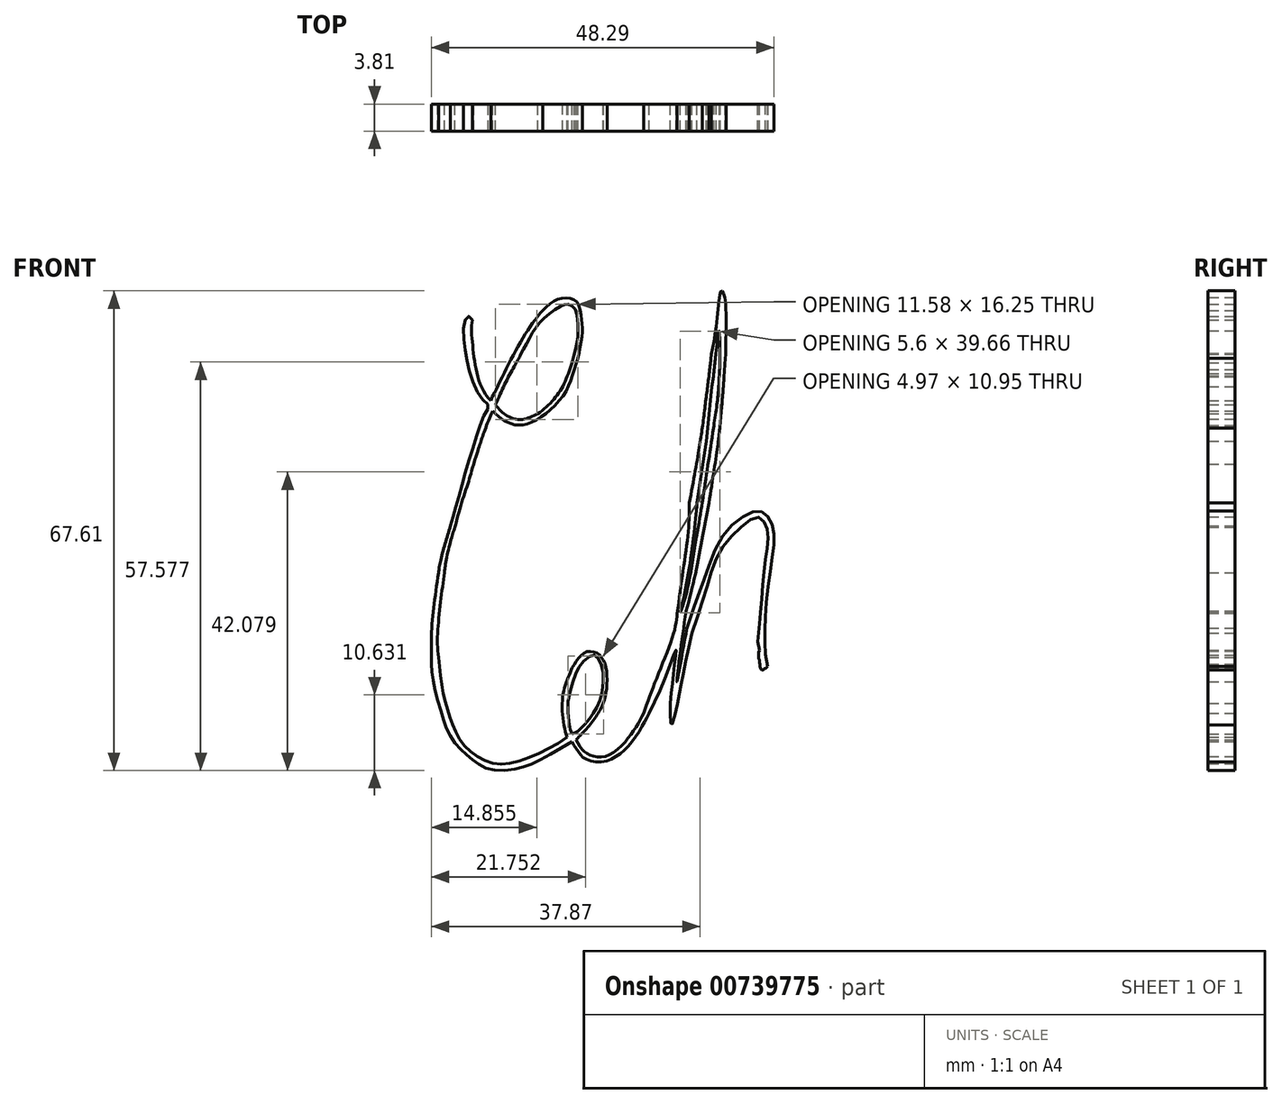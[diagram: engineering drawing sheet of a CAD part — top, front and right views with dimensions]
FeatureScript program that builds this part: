
annotation { "Feature Type Name" : "Feature", "Feature Type Description" : "" }
export const myFeature = defineFeature(function(context is Context, id is Id, definition is map)
    precondition{}
    {
        {
            var Q0;
            Q0=qCreatedBy(makeId("Front.planeOp"),FACE);
            var sketch = newSketch(context, id + "F0", { "sketchPlane" : qUnion([Q0])});
            skFitSpline(sketch, "E0", {"points": [v(-64.35, 36.4) * mm, v(-64.4, 33.61) * mm, v(-63.78, 29.13) * mm, v(-61.8, 25.09) * mm], "startDerivative": vector(-2.62, -8.07) * mm, "endDerivative": vector(9.26, -9.07) * mm});
            skFitSpline(sketch, "E1", {"points": [v(-64.35, 36.4) * mm, v(-64.98, 36.94) * mm, v(-65.59, 35.64) * mm, v(-65.34, 32.1) * mm, v(-64.6, 28.52) * mm, v(-62.99, 25.26) * mm, v(-62.14, 24.35) * mm, v(-62.62, 23.14) * mm, v(-63.9, 19.7) * mm, v(-65.4, 14.73) * mm, v(-66.62, 10.38) * mm, v(-67.46, 7.41) * mm], "startDerivative": vector(-16.96, 17.03) * mm, "endDerivative": vector(-8.5, -29.3) * mm});
            skFitSpline(sketch, "E2", {"points": [v(-61.8, 25.09) * mm, v(-59.74, 29.26) * mm, v(-56.96, 34.37) * mm, v(-54.45, 37.79) * mm], "startDerivative": vector(5.82, 11.78) * mm, "endDerivative": vector(8.75, 9.95) * mm});
            skFitSpline(sketch, "E3", {"points": [v(-61.53, 23.57) * mm, v(-62.96, 19.97) * mm, v(-64.2, 16.13) * mm], "startDerivative": vector(-3.47, -7.39) * mm, "endDerivative": vector(-4.23, -13.44) * mm});
            skFitSpline(sketch, "E4", {"points": [v(-64.2, 16.13) * mm, v(-64.92, 13.64) * mm, v(-65.9, 10.66) * mm, v(-66.63, 8.04) * mm, v(-66.83, 7.2) * mm], "startDerivative": vector(-3.72, -12.5) * mm, "endDerivative": vector(-1.05, -4.59) * mm});
            skFitSpline(sketch, "E5", {"points": [v(-61.1, 24.48) * mm, v(-59.66, 27.69) * mm, v(-58.31, 30.15) * mm, v(-57.6, 31.45) * mm], "startDerivative": vector(3.5, 8.33) * mm, "endDerivative": vector(2.51, 4.74) * mm});
            skFitSpline(sketch, "E6", {"points": [v(-61.1, 24.48) * mm, v(-59.62, 23) * mm, v(-57.22, 22.4) * mm, v(-55.13, 23.2) * mm], "startDerivative": vector(4.05, -5.34) * mm, "endDerivative": vector(6.73, 2.03) * mm});
            skFitSpline(sketch, "E7", {"points": [v(-61.53, 23.57) * mm, v(-60.22, 22.47) * mm, v(-58.91, 21.78) * mm, v(-57.12, 21.66) * mm, v(-54.44, 22.94) * mm, v(-51.5, 25.91) * mm, v(-50.02, 29.46) * mm], "startDerivative": vector(9.66, -8.64) * mm, "endDerivative": vector(5.16, 19.12) * mm});
            skFitSpline(sketch, "E8", {"points": [v(-55.13, 23.2) * mm, v(-52.99, 25.14) * mm, v(-51.45, 27.47) * mm, v(-50.36, 30.38) * mm], "startDerivative": vector(6.93, 4.81) * mm, "endDerivative": vector(2.85, 8.56) * mm});
            skFitSpline(sketch, "E9", {"points": [v(-57.6, 31.45) * mm, v(-56.5, 33.56) * mm, v(-55.39, 35.43) * mm, v(-53.75, 37.14) * mm, v(-51.86, 38.42) * mm, v(-50.98, 38.63) * mm, v(-50.06, 38.2) * mm, v(-49.63, 36.89) * mm, v(-49.5, 35.16) * mm, v(-49.65, 33.16) * mm, v(-50.36, 30.38) * mm], "startDerivative": vector(9.87, 18.84) * mm, "endDerivative": vector(-6.78, -23.18) * mm});
            skFitSpline(sketch, "E10", {"points": [v(-54.45, 37.79) * mm, v(-52.67, 39.23) * mm, v(-50.98, 39.51) * mm, v(-49.63, 38.95) * mm, v(-49.03, 36.89) * mm, v(-48.88, 35.06) * mm, v(-49.18, 32.77) * mm, v(-50.02, 29.46) * mm], "startDerivative": vector(11.6, 11.5) * mm, "endDerivative": vector(-7.3, -17.15) * mm});
            skFitSpline(sketch, "E11", {"points": [v(-67.46, 7.41) * mm, v(-66.83, 7.2) * mm], "startDerivative": vector(0.63, -0.2) * mm, "endDerivative": vector(0.63, -0.2) * mm});
            skFitSpline(sketch, "E12", {"points": [v(-67.46, 7.41) * mm, v(-68.32, 4.56) * mm, v(-68.98, 1.92) * mm, v(-69.14, 0.83) * mm], "startDerivative": vector(-2.23, -7.16) * mm, "endDerivative": vector(-0.43, -4.1) * mm});
            skFitSpline(sketch, "E13", {"points": [v(-66.83, 7.2) * mm, v(-67.46, 5.2) * mm, v(-68.2, 1.84) * mm, v(-68.3, 0.83) * mm], "startDerivative": vector(-1.82, -5.25) * mm, "endDerivative": vector(-0.2, -3.57) * mm});
            skFitSpline(sketch, "E14", {"points": [v(-69.14, 0.83) * mm, v(-69.73, -3.34) * mm, v(-70.1, -6.73) * mm, v(-70.16, -10.09) * mm, v(-70.13, -12.11) * mm], "startDerivative": vector(-2.2, -14.98) * mm, "endDerivative": vector(0.18, -9.47) * mm});
            skFitSpline(sketch, "E15", {"points": [v(-68.3, 0.83) * mm, v(-68.7, -2.07) * mm, v(-69.1, -5.55) * mm, v(-69.3, -8.6) * mm, v(-69.14, -11.16) * mm], "startDerivative": vector(-1.7, -11.4) * mm, "endDerivative": vector(1.4, -10.98) * mm});
            skFitSpline(sketch, "E16", {"points": [v(-70.13, -12.11) * mm, v(-69.84, -14.78) * mm, v(-68.75, -18.95) * mm, v(-67.7, -21.88) * mm, v(-65.97, -24.15) * mm, v(-64.15, -25.73) * mm, v(-61.95, -26.9) * mm, v(-58.2, -26.85) * mm, v(-55.23, -25.79) * mm, v(-50.33, -23) * mm], "startDerivative": vector(1.26, -23.58) * mm, "endDerivative": vector(35.66, 20.71) * mm});
            skFitSpline(sketch, "E17", {"points": [v(-69.14, -11.16) * mm, v(-68.72, -14.84) * mm, v(-67.97, -18.25) * mm, v(-67.06, -20.89) * mm, v(-65.58, -23.49) * mm, v(-62.94, -25.51) * mm, v(-59.95, -26.18) * mm, v(-55.65, -24.94) * mm, v(-51.03, -22.4) * mm], "startDerivative": vector(2.52, -29.28) * mm, "endDerivative": vector(28.6, 20.85) * mm});
            skFitSpline(sketch, "E18", {"points": [v(-51.03, -22.4) * mm, v(-50.33, -23) * mm], "startDerivative": vector(0.6, -0.6) * mm, "endDerivative": vector(0.6, -0.6) * mm});
            skFitSpline(sketch, "E19", {"points": [v(-51.03, -22.4) * mm, v(-51.62, -19.7) * mm, v(-51.6, -16.4) * mm, v(-51.03, -14.36) * mm, v(-50.34, -12.6) * mm], "startDerivative": vector(-2.82, 8.16) * mm, "endDerivative": vector(2.45, 7.62) * mm});
            skFitSpline(sketch, "E20", {"points": [v(-50.33, -21.92) * mm, v(-50.66, -20.9) * mm, v(-50.91, -17.6) * mm, v(-50.05, -14.13) * mm, v(-49.2, -12.27) * mm, v(-47.68, -10.9) * mm, v(-47.04, -10.88) * mm, v(-46.2, -12.12) * mm, v(-45.95, -14.65) * mm, v(-46.59, -17.62) * mm, v(-47.44, -19.13) * mm, v(-48.62, -20.67) * mm, v(-50.33, -21.92) * mm]});
            skFitSpline(sketch, "E21", {"points": [v(-50.34, -12.6) * mm, v(-49.45, -11.32) * mm, v(-48.35, -10.38) * mm, v(-47.11, -10.4) * mm, v(-46.24, -11.04) * mm, v(-45.64, -12.27) * mm, v(-45.4, -14.17) * mm, v(-45.55, -16.11) * mm, v(-45.95, -17.62) * mm], "startDerivative": vector(6.67, 10.14) * mm, "endDerivative": vector(-4.17, -10.58) * mm});
            skFitSpline(sketch, "E22", {"points": [v(-45.95, -17.62) * mm, v(-46.92, -19.43) * mm, v(-48.07, -20.98) * mm, v(-49.17, -22.13) * mm, v(-49.79, -22.74) * mm, v(-50.33, -23) * mm], "startDerivative": vector(-3.31, -8.04) * mm, "endDerivative": vector(-3.52, -1.93) * mm});
            skFitSpline(sketch, "E23", {"points": [v(-49.79, -22.74) * mm, v(-48.83, -24.24) * mm, v(-47.54, -25) * mm, v(-45.45, -25.05) * mm, v(-42.88, -23.06) * mm, v(-41.26, -20.86) * mm, v(-40.25, -19) * mm], "startDerivative": vector(5.87, -10.96) * mm, "endDerivative": vector(4.64, 10.81) * mm});
            skFitSpline(sketch, "E24", {"points": [v(-50.33, -23) * mm, v(-49.5, -24.38) * mm, v(-48.49, -25.41) * mm, v(-46.03, -25.84) * mm, v(-43.55, -24.7) * mm, v(-41.3, -22.2) * mm, v(-39.76, -19.6) * mm, v(-39.46, -19) * mm], "startDerivative": vector(5.98, -12.09) * mm, "endDerivative": vector(3.02, 5.95) * mm});
            skFitSpline(sketch, "E25", {"points": [v(-40.25, -19) * mm, v(-39.46, -19) * mm], "startDerivative": vector(0.86, 0) * mm, "endDerivative": vector(0.86, 0) * mm});
            skFitSpline(sketch, "E26", {"points": [v(-39.46, -19) * mm, v(-37.02, -13.56) * mm, v(-35.69, -10.1) * mm, v(-35.83, -11.76) * mm, v(-36.2, -14.82) * mm, v(-36.52, -18.64) * mm, v(-36.34, -20.65) * mm, v(-35.5, -17.8) * mm, v(-34.83, -14.21) * mm, v(-33.42, -7.73) * mm], "startDerivative": vector(17.31, 35.25) * mm, "endDerivative": vector(10.54, 46.96) * mm});
            skFitSpline(sketch, "E27", {"points": [v(-40.25, -19) * mm, v(-38.42, -14.1) * mm, v(-36.01, -7.73) * mm, v(-35.5, -4.93) * mm], "startDerivative": vector(4.73, 13.2) * mm, "endDerivative": vector(1.04, 9.73) * mm});
            skFitSpline(sketch, "E28", {"points": [v(-34.25, -4.6) * mm, v(-34.83, -8.45) * mm, v(-35.33, -12.3) * mm, v(-35.55, -14.6) * mm, v(-34.97, -11.44) * mm, v(-34.14, -7.02) * mm], "startDerivative": vector(-2.82, -18.55) * mm, "endDerivative": vector(3.5, 17.96) * mm});
            skFitSpline(sketch, "E29", {"points": [v(-33.42, -7.73) * mm, v(-34.14, -7.02) * mm], "startDerivative": vector(-0.72, 0.72) * mm, "endDerivative": vector(-0.72, 0.72) * mm});
            skFitSpline(sketch, "E30", {"points": [v(-35.5, -4.93) * mm, v(-34.25, -4.6) * mm], "startDerivative": vector(1.26, 0.32) * mm, "endDerivative": vector(1.26, 0.32) * mm});
            skFitSpline(sketch, "E31", {"points": [v(-35.5, -4.93) * mm, v(-34.63, 1.5) * mm, v(-33.93, 6.86) * mm, v(-33.81, 10.61) * mm], "startDerivative": vector(2.32, 17.43) * mm, "endDerivative": vector(0.05, 12.66) * mm});
            skFitSpline(sketch, "E32", {"points": [v(-35.1, -4.82) * mm, v(-34.17, -0.64) * mm, v(-33.5, 3.54) * mm, v(-33, 7.86) * mm, v(-32.72, 10.67) * mm], "startDerivative": vector(3.72, 16.02) * mm, "endDerivative": vector(1.14, 12.43) * mm});
            skFitSpline(sketch, "E33", {"points": [v(-35.1, -4.82) * mm, v(-34.26, -2.21) * mm, v(-33.2, 3.23) * mm, v(-32.45, 7.92) * mm, v(-31.97, 10.74) * mm], "startDerivative": vector(3.98, 11.11) * mm, "endDerivative": vector(2.19, 12.4) * mm});
            skFitSpline(sketch, "E34", {"points": [v(-34.25, -4.6) * mm, v(-33.02, 0.36) * mm, v(-31.97, 5.65) * mm, v(-31.06, 10.64) * mm], "startDerivative": vector(3.84, 14.83) * mm, "endDerivative": vector(2.7, 15) * mm});
            skFitSpline(sketch, "E35", {"points": [v(-31.97, 10.74) * mm, v(-30.85, 18.28) * mm, v(-30.42, 21.15) * mm], "startDerivative": vector(2.03, 13.64) * mm, "endDerivative": vector(0.98, 6.64) * mm});
            skFitSpline(sketch, "E36", {"points": [v(-31.06, 10.64) * mm, v(-29.88, 18.28) * mm, v(-29.52, 21.15) * mm], "startDerivative": vector(2.2, 13.78) * mm, "endDerivative": vector(0.78, 6.67) * mm});
            skFitSpline(sketch, "E37", {"points": [v(-32.72, 10.67) * mm, v(-31.42, 19.34) * mm], "startDerivative": vector(1.3, 8.66) * mm, "endDerivative": vector(1.3, 8.66) * mm});
            skFitSpline(sketch, "E38", {"points": [v(-33.81, 10.61) * mm, v(-32.48, 17.98) * mm, v(-31.97, 21.24) * mm], "startDerivative": vector(2.5, 13.48) * mm, "endDerivative": vector(1.1, 7.37) * mm});
            skFitSpline(sketch, "E39", {"points": [v(-31.42, 19.34) * mm, v(-31.2, 21.15) * mm], "startDerivative": vector(0.21, 1.82) * mm, "endDerivative": vector(0.21, 1.82) * mm});
            skFitSpline(sketch, "E40", {"points": [v(-30.42, 21.15) * mm, v(-29.52, 21.15) * mm], "startDerivative": vector(0.9, 0) * mm, "endDerivative": vector(0.9, 0) * mm});
            skFitSpline(sketch, "E41", {"points": [v(-31.97, 21.24) * mm, v(-31.2, 21.15) * mm], "startDerivative": vector(0.76, -0.1) * mm, "endDerivative": vector(0.76, -0.1) * mm});
            skFitSpline(sketch, "E42", {"points": [v(-31.2, 21.15) * mm, v(-30.64, 27.04) * mm], "startDerivative": vector(0.57, 5.88) * mm, "endDerivative": vector(0.57, 5.88) * mm});
            skFitSpline(sketch, "E43", {"points": [v(-31.97, 21.24) * mm, v(-31.46, 25.35) * mm, v(-31.05, 28.44) * mm], "startDerivative": vector(0.96, 7.94) * mm, "endDerivative": vector(0.86, 6.42) * mm});
            skFitSpline(sketch, "E44", {"points": [v(-30.42, 21.15) * mm, v(-29.8, 25.65) * mm, v(-29.58, 28.84) * mm], "startDerivative": vector(1.34, 8.62) * mm, "endDerivative": vector(0.32, 6.69) * mm});
            skFitSpline(sketch, "E45", {"points": [v(-29.52, 21.15) * mm, v(-29.15, 25.44) * mm, v(-28.93, 28.39) * mm], "startDerivative": vector(0.73, 8.2) * mm, "endDerivative": vector(0.43, 6.2) * mm});
            skFitSpline(sketch, "E46", {"points": [v(-30.64, 27.04) * mm, v(-30.42, 28.48) * mm], "startDerivative": vector(0.22, 1.44) * mm, "endDerivative": vector(0.22, 1.44) * mm});
            skFitSpline(sketch, "E47", {"points": [v(-30.42, 28.48) * mm, v(-31.05, 28.44) * mm], "startDerivative": vector(-0.63, -0.04) * mm, "endDerivative": vector(-0.63, -0.04) * mm});
            skFitSpline(sketch, "E48", {"points": [v(-29.58, 28.84) * mm, v(-28.93, 28.39) * mm], "startDerivative": vector(0.65, -0.45) * mm, "endDerivative": vector(0.65, -0.45) * mm});
            skFitSpline(sketch, "E49", {"points": [v(-30.42, 28.48) * mm, v(-30.16, 30.82) * mm, v(-30.06, 31.64) * mm], "startDerivative": vector(0.47, 4.2) * mm, "endDerivative": vector(0.23, 1.93) * mm});
            skFitSpline(sketch, "E50", {"points": [v(-29.58, 28.84) * mm, v(-29.5, 30.49) * mm, v(-29.5, 31.64) * mm], "startDerivative": vector(0.2, 3.16) * mm, "endDerivative": vector(-0.03, 2.42) * mm});
            skFitSpline(sketch, "E51", {"points": [v(-31.05, 28.44) * mm, v(-30.76, 31.1) * mm, v(-30.71, 31.62) * mm], "startDerivative": vector(0.52, 4.58) * mm, "endDerivative": vector(0.1, 1.36) * mm});
            skFitSpline(sketch, "E52", {"points": [v(-28.93, 28.39) * mm, v(-28.73, 31.04) * mm], "startDerivative": vector(0.2, 2.66) * mm, "endDerivative": vector(0.2, 2.66) * mm});
            skFitSpline(sketch, "E53", {"points": [v(-30.06, 31.64) * mm, v(-29.64, 34.9) * mm, v(-29.53, 33.9) * mm, v(-29.5, 31.64) * mm], "startDerivative": vector(1.17, 11.6) * mm, "endDerivative": vector(0.02, -6.52) * mm});
            skFitSpline(sketch, "E54", {"points": [v(-30.71, 31.62) * mm, v(-30.06, 35.34) * mm, v(-29.5, 40.13) * mm, v(-29.28, 40.54) * mm, v(-28.95, 40.13) * mm, v(-28.65, 38.1) * mm, v(-28.64, 35.11) * mm, v(-28.67, 32.38) * mm, v(-28.73, 31.04) * mm], "startDerivative": vector(4.1, 19.52) * mm, "endDerivative": vector(-2.58, -8.46) * mm});
            skFitSpline(sketch, "E55", {"points": [v(-34.14, -7.02) * mm, v(-31.67, 0) * mm, v(-29.2, 5.9) * mm, v(-25.64, 9.03) * mm, v(-23.62, 9.4) * mm, v(-22.35, 8.07) * mm, v(-21.87, 5.7) * mm, v(-22.3, 1.78) * mm, v(-23.01, -4.28) * mm, v(-23.14, -8.73) * mm, v(-22.77, -12.38) * mm], "startDerivative": vector(28.4, 88.34) * mm, "endDerivative": vector(11.15, -39.79) * mm});
            skFitSpline(sketch, "E56", {"points": [v(-33.42, -7.73) * mm, v(-31.29, -1.04) * mm, v(-29.38, 4) * mm, v(-26.32, 7.41) * mm, v(-24.02, 8.63) * mm, v(-23.12, 7.7) * mm, v(-22.69, 5.9) * mm, v(-23.05, 2.88) * mm, v(-23.48, -1.37) * mm, v(-23.88, -5.94) * mm, v(-24.1, -8.1) * mm, v(-23.95, -10.14) * mm], "startDerivative": vector(16.84, 51.55) * mm, "endDerivative": vector(14.69, -23.5) * mm});
            skFitSpline(sketch, "E57", {"points": [v(-23.95, -10.14) * mm, v(-23.95, -11.55) * mm, v(-23.66, -12.86) * mm, v(-22.77, -12.38) * mm], "startDerivative": vector(-2.06, -8.34) * mm, "endDerivative": vector(3.13, 3.2) * mm});
            skSolve(sketch);
        }
        {
            var Q0;
            Q0 = qSketchRegion(id + "F0", true);
            extrude(context, id + "F1", {"entities" : qUnion([Q0]), "depth" : 3.8 * mm, "offsetDistance" : 25.4 * mm});
        }
    });
